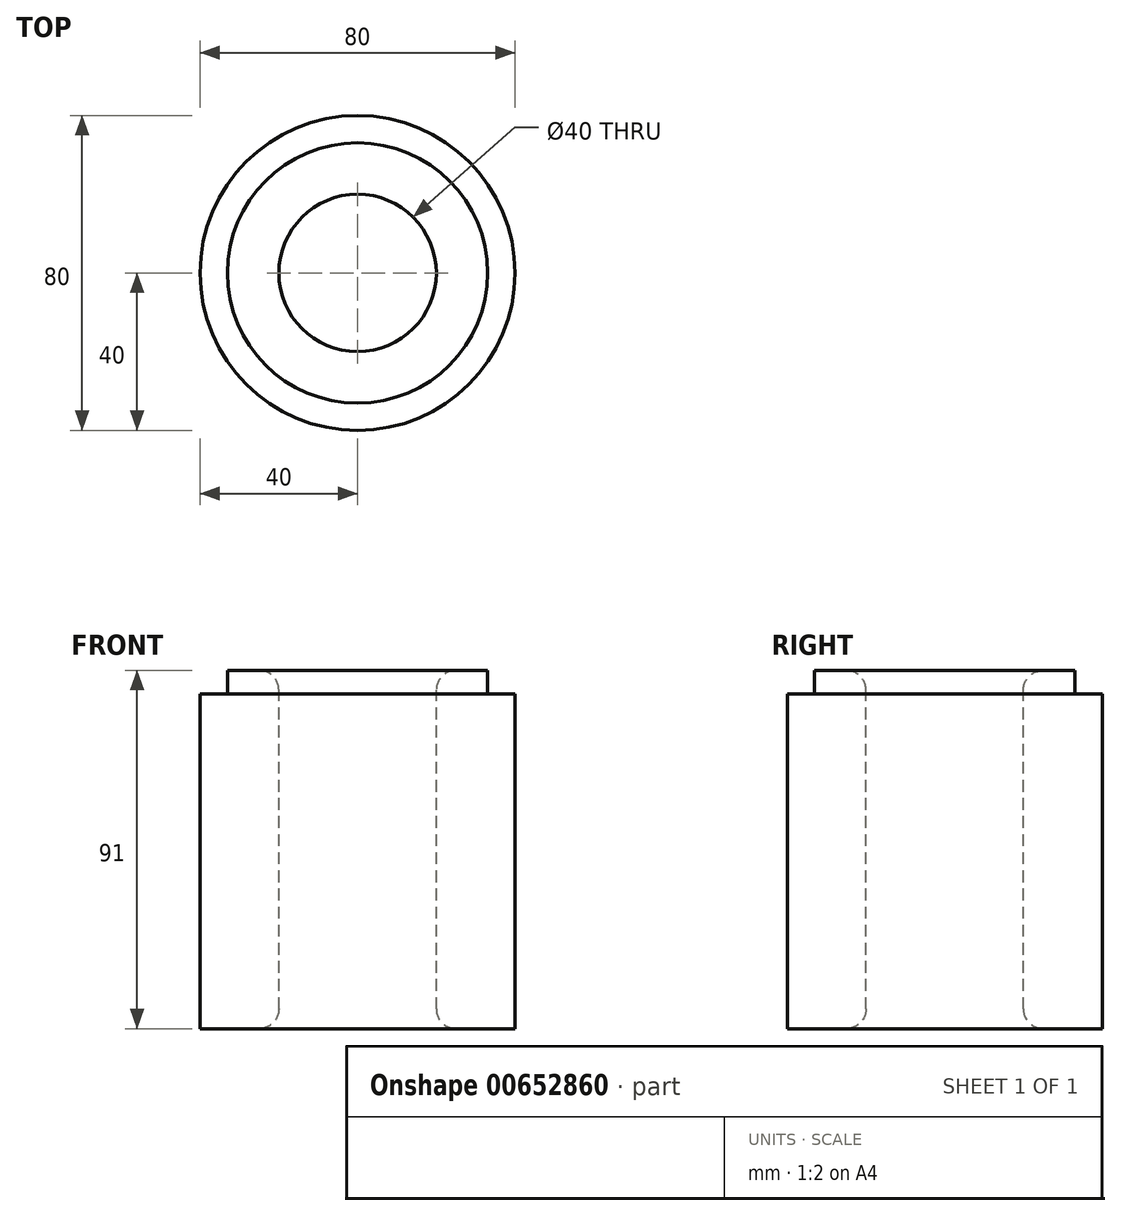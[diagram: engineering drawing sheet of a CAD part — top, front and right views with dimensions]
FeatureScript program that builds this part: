
annotation { "Feature Type Name" : "Feature", "Feature Type Description" : "" }
export const myFeature = defineFeature(function(context is Context, id is Id, definition is map)
    precondition{}
    {
        {
            var Q0;
            Q0=qCreatedBy(makeId("Top.planeOp"),FACE);
            var sketch = newSketch(context, id + "F0", { "sketchPlane" : qUnion([Q0])});
            skCircle(sketch, "E0", {"center": v(0, 0) * mm, "radius": 40 * mm});
            skSolve(sketch);
        }
        {
            var Q0;
            Q0=qSketchRegion(id+"F0",true);
            extrude(context, id + "F1", {"entities" : qUnion([Q0]), "depth" : 85 * mm, "offsetDistance" : 25 * mm});
        }
        {
            var Q0;
            Q0=makeQuery(id+"F1.opExtrude","CAP_FACE",FACE,{"disambiguationData":[OSD([sQuery(id+"F0.wireOp",EDGE,"E0")])],"isStart":false});
            var sketch = newSketch(context, id + "F2", { "sketchPlane" : qUnion([Q0])});
            skCircle(sketch, "E1", {"center": v(0, 0) * mm, "radius": 20 * mm});
            skSolve(sketch);
        }
        {
            var Q0;
            Q0=makeQuery(id+"F2.imprint","IMPRINT",FACE,{"disambiguationData":[TD([[makeQuery(id+"F2.imprint","IMPRINT",EDGE,{"derivedFrom":sQuery(id+"F2.wireOp",EDGE,"E1")}),1.0]])]});
            extrude(context, id + "F3", {"entities" : qUnion([Q0]), "operationType" : NewBodyOperationType.REMOVE, "oppositeDirection" : true, "depth" : 88 * mm, "offsetDistance" : 25 * mm});
        }
        {
            var Q0;
            Q0=makeQuery(id+"F3.boolean.opBoolean","INTERSECT",EDGE,{"derivedFrom":[makeQuery(id+"F1.opExtrude","CAP_FACE",FACE,{"disambiguationData":[OSD([sQuery(id+"F0.wireOp",EDGE,"E0")])],"isStart":true}),makeQuery(id+"F3.opExtrude","SWEPT_FACE",FACE,{"disambiguationData":[OSD([sQuery(id+"F2.wireOp",EDGE,"E1")])]})]});
            fillet(context, id + "F4", {"entities" : qUnion([Q0]), "radius" : 5 * mm, "tangentPropagation" : true, "allowEdgeOverflow" : false});
        }
        {
            var Q0;
            Q0=makeQuery(id+"F1.opExtrude","CAP_FACE",FACE,{"disambiguationData":[OSD([sQuery(id+"F0.wireOp",EDGE,"E0")])],"isStart":false});
            var sketch = newSketch(context, id + "F5", { "sketchPlane" : qUnion([Q0])});
            skCircle(sketch, "E2", {"center": v(0, 0) * mm, "radius": 33.06 * mm});
            skSolve(sketch);
        }
        {
            var Q0;
            Q0=makeQuery(id+"F5.imprint","IMPRINT",FACE,{"disambiguationData":[TD([[makeQuery(id+"F5.imprint","IMPRINT",EDGE,{"derivedFrom":sQuery(id+"F5.wireOp",EDGE,"E2")}),1.0]])]});
            extrude(context, id + "F6", {"entities" : qUnion([Q0]), "operationType" : NewBodyOperationType.ADD, "endBound" : BoundingType.SYMMETRIC, "depth" : 12 * mm, "offsetDistance" : 25 * mm});
        }
        {
            var Q0;
            {var subQ0=sQuery(id+"F2.wireOp",EDGE,"E1");Q0=makeQuery(id+"F6.boolean.opBoolean","MERGE",FACE,{"derivedFrom":[makeQuery(id+"F3.boolean.opBoolean","COPY",FACE,{"derivedFrom":makeQuery(id+"F3.opExtrude","SWEPT_FACE",FACE,{"disambiguationData":[OSD([subQ0])]})}),makeQuery(id+"F6.opExtrude","SWEPT_FACE",FACE,{"disambiguationData":[OSD([subQ0])]})]});}
            fillet(context, id + "F7", {"entities" : qUnion([Q0]), "radius" : 5 * mm, "tangentPropagation" : true, "allowEdgeOverflow" : false});
        }
    });
